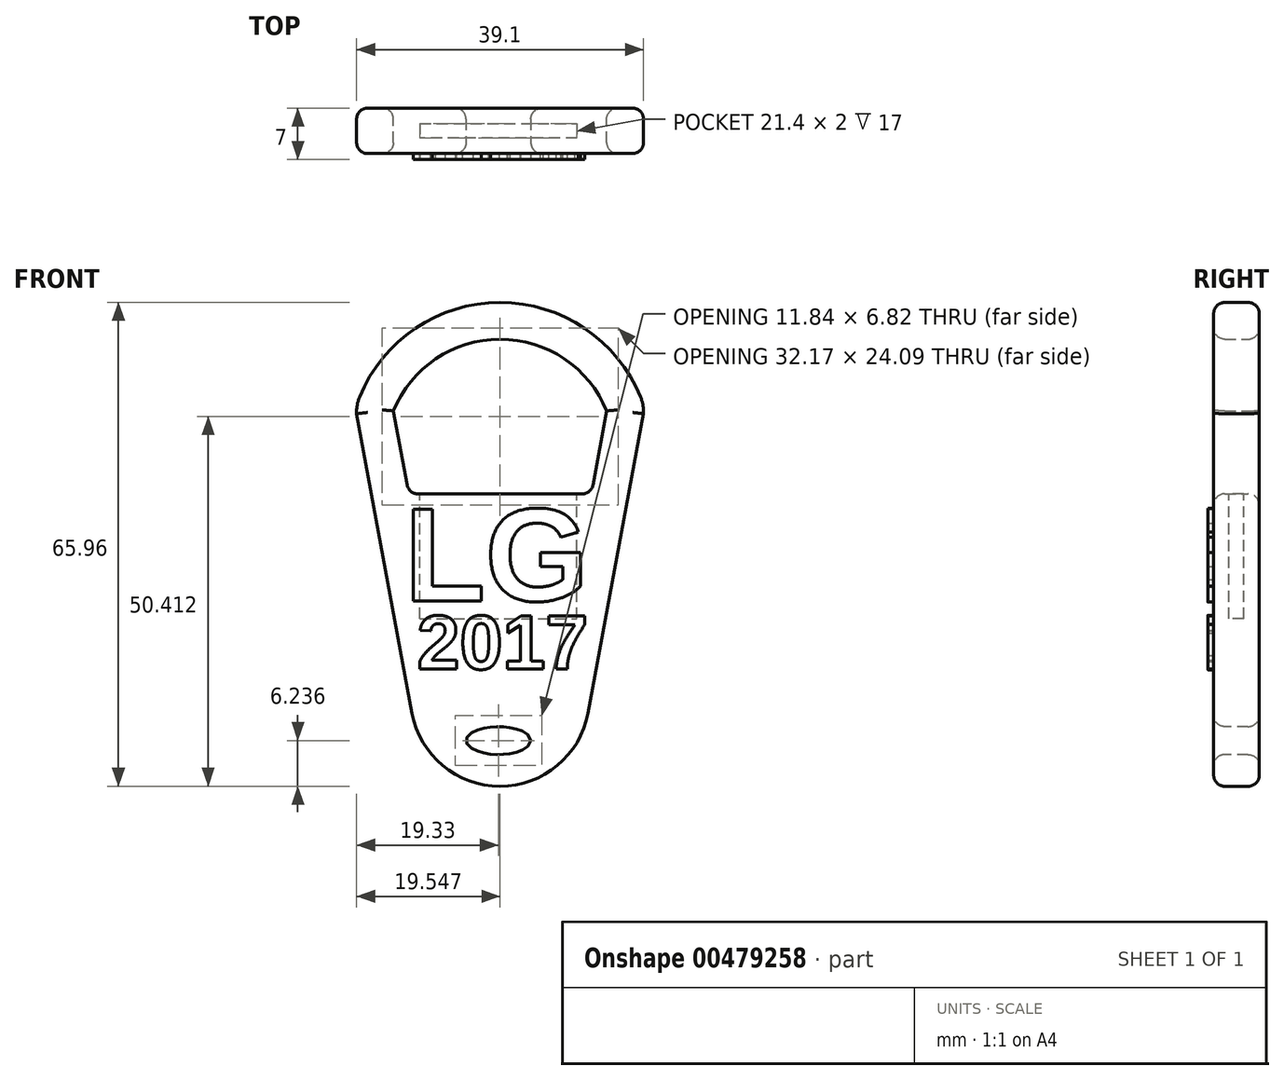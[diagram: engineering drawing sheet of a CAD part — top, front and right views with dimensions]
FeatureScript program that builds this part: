
annotation { "Feature Type Name" : "Feature", "Feature Type Description" : "" }
export const myFeature = defineFeature(function(context is Context, id is Id, definition is map)
    precondition{}
    {
        {
            var Q0;
            Q0=qCreatedBy(makeId("Front.planeOp"),FACE);
            var sketch = newSketch(context, id + "F0", { "sketchPlane" : qUnion([Q0])});
            skLineSegment(sketch, "E0", {"start": v(0.22, 53.5) * mm, "end": v(0.22, -27.22) * mm, "construction": true});
            skLineSegment(sketch, "E1", {"start": v(19.76, 12.33) * mm, "end": v(12.22, -28.48) * mm});
            skLineSegment(sketch, "E2.MirrorCS", {"start": v(-19.33, 12.33) * mm, "end": v(-11.78, -28.48) * mm});
            skLineSegment(sketch, "E3.0", {"start": v(-14.31, 12.71) * mm, "end": v(-12.22, 1.4) * mm});
            skLineSegment(sketch, "E3.3", {"start": v(14.75, 12.71) * mm, "end": v(12.66, 1.4) * mm});
            skLineSegment(sketch, "E4", {"start": v(-12.22, 1.4) * mm, "end": v(12.66, 1.4) * mm});
            skPoint(sketch, "E5", {"position": v(0.22, 20.6) * mm});
            skPoint(sketch, "E6", {"position": v(-14.31, 12.71) * mm});
            skPoint(sketch, "E7.MirrorP", {"position": v(14.75, 12.71) * mm});
            skArc(sketch, "E8", {"start": v(14.75, 12.71) * mm, "mid": v(0.22, 22.5) * mm, "end": v(-14.31, 12.71) * mm});
            skArc(sketch, "E9.0", {"start": v(19.62, 13.97) * mm, "mid": v(0.56, 27.5) * mm, "end": v(-18.94, 14.6) * mm});
            skArc(sketch, "E10", {"start": v(-18.94, 14.6) * mm, "mid": v(-19.26, 13.5) * mm, "end": v(-19.33, 12.33) * mm});
            skArc(sketch, "E11.MirrorCS", {"start": v(19.38, 14.6) * mm, "mid": v(19.7, 13.5) * mm, "end": v(19.76, 12.33) * mm});
            skPoint(sketch, "E12.orphan", {"position": v(-21.9, 26.19) * mm});
            skPoint(sketch, "E13.orphan", {"position": v(22.32, 26.19) * mm});
            skPoint(sketch, "E14.MirrorCS.start.orphan", {"position": v(0.22, 25.6) * mm});
            skArc(sketch, "E15", {"start": v(-11.78, -28.48) * mm, "mid": v(0.22, -38.46) * mm, "end": v(12.22, -28.48) * mm});
            skPoint(sketch, "E16.MirrorCS.end.orphan", {"position": v(0.22, -28.48) * mm});
            skPoint(sketch, "E16.MirrorCS.start.orphan", {"position": v(-11.78, -28.48) * mm});
            skLineSegment(sketch, "E17", {"start": v(-11.78, -28.48) * mm, "end": v(12.22, -28.48) * mm, "construction": true});
            skSolve(sketch);
        }
        {
            var Q0;
            Q0=qSketchRegion(id+"F0",true);
            extrude(context, id + "F1", {"entities" : qUnion([Q0]), "depth" : 6.2 * mm});
        }
        {
            var Q0;
            Q0=makeQuery(id+"F1.opExtrude","CAP_FACE",FACE,{"disambiguationData":[OSD([sQuery(id+"F0.wireOp",EDGE,"E1"),sQuery(id+"F0.wireOp",EDGE,"E2.MirrorCS"),sQuery(id+"F0.wireOp",EDGE,"E3.0"),sQuery(id+"F0.wireOp",EDGE,"E3.3"),sQuery(id+"F0.wireOp",EDGE,"E4"),sQuery(id+"F0.wireOp",EDGE,"E8"),sQuery(id+"F0.wireOp",EDGE,"E9.0"),sQuery(id+"F0.wireOp",EDGE,"E10"),sQuery(id+"F0.wireOp",EDGE,"E11.MirrorCS"),sQuery(id+"F0.wireOp",EDGE,"E15")])],"isStart":false});
            var sketch = newSketch(context, id + "F2", { "sketchPlane" : qUnion([Q0])});
            skEllipse(sketch, "E18", {"center": v(0, -32.22) * mm, "majorRadius": 4.42 * mm, "minorRadius": 1.9 * mm, "majorAxis": v(1, 0)});
            skSolve(sketch);
        }
        {
            var Q0;
            Q0=makeQuery(id+"F2.imprint","IMPRINT",FACE,{"disambiguationData":[TD([[makeQuery(id+"F2.imprint","IMPRINT",EDGE,{"derivedFrom":sQuery(id+"F2.wireOp",EDGE,"E18")}),1.0]])]});
            extrude(context, id + "F3", {"entities" : qUnion([Q0]), "operationType" : NewBodyOperationType.REMOVE, "oppositeDirection" : true, "depth" : 6.5 * mm});
        }
        {
            var Q0;
            Q0=makeQuery(id+"F1.opExtrude","SWEPT_FACE",FACE,{"disambiguationData":[OSD([sQuery(id+"F0.wireOp",EDGE,"E4")])]});
            var sketch = newSketch(context, id + "F4", { "sketchPlane" : qUnion([Q0])});
            skLineSegment(sketch, "E19", {"start": v(0, -2.1) * mm, "end": v(10.7, -2.1) * mm});
            skLineSegment(sketch, "E20.0", {"start": v(0, -4.1) * mm, "end": v(10.7, -4.1) * mm});
            skLineSegment(sketch, "E21", {"start": v(10.7, -2.1) * mm, "end": v(10.7, -4.1) * mm});
            skLineSegment(sketch, "E22", {"start": v(0, -2.1) * mm, "end": v(0, -4.1) * mm, "construction": true});
            skLineSegment(sketch, "E23.MirrorCS", {"start": v(0, -2.1) * mm, "end": v(-10.7, -2.1) * mm});
            skLineSegment(sketch, "E24.MirrorCS", {"start": v(-10.7, -2.1) * mm, "end": v(-10.7, -4.1) * mm});
            skLineSegment(sketch, "E25.MirrorCS", {"start": v(0, -4.1) * mm, "end": v(-10.7, -4.1) * mm});
            skSolve(sketch);
        }
        {
            var Q0;
            Q0=makeQuery(id+"F4.imprint","IMPRINT",FACE,{"disambiguationData":[TD([[makeQuery(id+"F4.imprint","IMPRINT",EDGE,{"derivedFrom":sQuery(id+"F4.wireOp",EDGE,"E19")}),-1.0]])]});
            extrude(context, id + "F5", {"entities" : qUnion([Q0]), "operationType" : NewBodyOperationType.REMOVE, "oppositeDirection" : true, "depth" : 17 * mm});
        }
        {
            var Q0;
            Q0=makeQuery(id+"F1.opExtrude","SWEPT_EDGE",EDGE,{"disambiguationData":[OSD([sQuery(id+"F0.wireOp",EDGE,"E3.0"),sQuery(id+"F0.wireOp",EDGE,"E4")])]});
            var Q1;
            Q1=makeQuery(id+"F1.opExtrude","SWEPT_EDGE",EDGE,{"disambiguationData":[OSD([sQuery(id+"F0.wireOp",EDGE,"E3.3"),sQuery(id+"F0.wireOp",EDGE,"E4")])]});
            var Q2;
            Q2=makeQuery(id+"F1.opExtrude","CAP_FACE",FACE,{"disambiguationData":[OSD([sQuery(id+"F0.wireOp",EDGE,"E1"),sQuery(id+"F0.wireOp",EDGE,"E2.MirrorCS"),sQuery(id+"F0.wireOp",EDGE,"E3.0"),sQuery(id+"F0.wireOp",EDGE,"E3.3"),sQuery(id+"F0.wireOp",EDGE,"E4"),sQuery(id+"F0.wireOp",EDGE,"E8"),sQuery(id+"F0.wireOp",EDGE,"E9.0"),sQuery(id+"F0.wireOp",EDGE,"E10"),sQuery(id+"F0.wireOp",EDGE,"E11.MirrorCS"),sQuery(id+"F0.wireOp",EDGE,"E15")])],"isStart":false});
            var Q3;
            Q3=makeQuery(id+"F1.opExtrude","CAP_FACE",FACE,{"disambiguationData":[OSD([sQuery(id+"F0.wireOp",EDGE,"E1"),sQuery(id+"F0.wireOp",EDGE,"E2.MirrorCS"),sQuery(id+"F0.wireOp",EDGE,"E3.0"),sQuery(id+"F0.wireOp",EDGE,"E3.3"),sQuery(id+"F0.wireOp",EDGE,"E4"),sQuery(id+"F0.wireOp",EDGE,"E8"),sQuery(id+"F0.wireOp",EDGE,"E9.0"),sQuery(id+"F0.wireOp",EDGE,"E10"),sQuery(id+"F0.wireOp",EDGE,"E11.MirrorCS"),sQuery(id+"F0.wireOp",EDGE,"E15")])],"isStart":true});
            fillet(context, id + "F6", {"entities" : qUnion([Q0, Q1, Q2, Q3]), "radius" : 1.5 * mm, "tangentPropagation" : true, "allowEdgeOverflow" : false});
        }
        {
            var Q0;
            Q0=makeQuery(id+"F1.opExtrude","CAP_FACE",FACE,{"disambiguationData":[OSD([sQuery(id+"F0.wireOp",EDGE,"E1"),sQuery(id+"F0.wireOp",EDGE,"E2.MirrorCS"),sQuery(id+"F0.wireOp",EDGE,"E3.0"),sQuery(id+"F0.wireOp",EDGE,"E3.3"),sQuery(id+"F0.wireOp",EDGE,"E4"),sQuery(id+"F0.wireOp",EDGE,"E8"),sQuery(id+"F0.wireOp",EDGE,"E9.0"),sQuery(id+"F0.wireOp",EDGE,"E10"),sQuery(id+"F0.wireOp",EDGE,"E11.MirrorCS"),sQuery(id+"F0.wireOp",EDGE,"E15")])],"isStart":false});
            var sketch = newSketch(context, id + "F7", { "sketchPlane" : qUnion([Q0])});
            skText(sketch, "E26", { "text": "LG", "fontName": "Arimo-Bold.ttf"});
            const initialGuessF7  = {"E26": [-0.01285, -0.01317, 1, 0, 0.01303]};
            skSetInitialGuess(sketch, initialGuessF7);
            skSolve(sketch);
        }
        {
            var Q0;
            Q0 = qSketchRegion(id + "F7", true);
            extrude(context, id + "F8", {"entities" : qUnion([Q0]), "operationType" : NewBodyOperationType.ADD, "depth" : .8 * mm, "offsetDistance" : 25 * mm});
        }
        {
            var Q0;
            Q0=makeQuery(id+"F1.opExtrude","CAP_FACE",FACE,{"disambiguationData":[OSD([sQuery(id+"F0.wireOp",EDGE,"E1"),sQuery(id+"F0.wireOp",EDGE,"E2.MirrorCS"),sQuery(id+"F0.wireOp",EDGE,"E3.0"),sQuery(id+"F0.wireOp",EDGE,"E3.3"),sQuery(id+"F0.wireOp",EDGE,"E4"),sQuery(id+"F0.wireOp",EDGE,"E8"),sQuery(id+"F0.wireOp",EDGE,"E9.0"),sQuery(id+"F0.wireOp",EDGE,"E10"),sQuery(id+"F0.wireOp",EDGE,"E11.MirrorCS"),sQuery(id+"F0.wireOp",EDGE,"E15")])],"isStart":false});
            var sketch = newSketch(context, id + "F9", { "sketchPlane" : qUnion([Q0])});
            skText(sketch, "E27", { "text": "2017", "fontName": "Arimo-Bold.ttf"});
            const initialGuessF9  = {"E27": [-0.0111, -0.02247, 1, 0, 0.00755]};
            skSetInitialGuess(sketch, initialGuessF9);
            skSolve(sketch);
        }
        {
            var Q0;
            Q0 = qSketchRegion(id + "F9", true);
            extrude(context, id + "F10", {"entities" : qUnion([Q0]), "operationType" : NewBodyOperationType.ADD, "depth" : .8 * mm, "offsetDistance" : 25 * mm});
        }
    });
